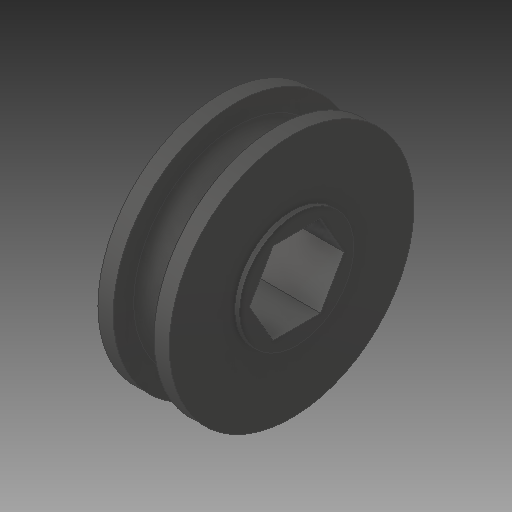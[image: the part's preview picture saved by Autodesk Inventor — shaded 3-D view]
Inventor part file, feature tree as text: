
AUTODESK INVENTOR PART (.ipt)
format: ipt  version: 2018 (Build 220112000, 112)  size: 160,256 bytes
history: native  units: in
note: dims shown in document units (in); Inventor stores cm internally (conversion verified against a paired STEP export)
features: fillet x1
ambient origin geometry x8: Origin, YZ Plane, XZ Plane, XY Plane, X Axis, Y Axis, Z Axis, Center Point
bodies: Solid1 (feature_tree)
feature tree (1):
  fillet  "Fillet1"  [1 undecoded]
note: 1 required parameter value undecoded (feature->parameter linkage not recoverable at this tier; creation-order binding heuristic only, values carry confidence <= 0.55)
